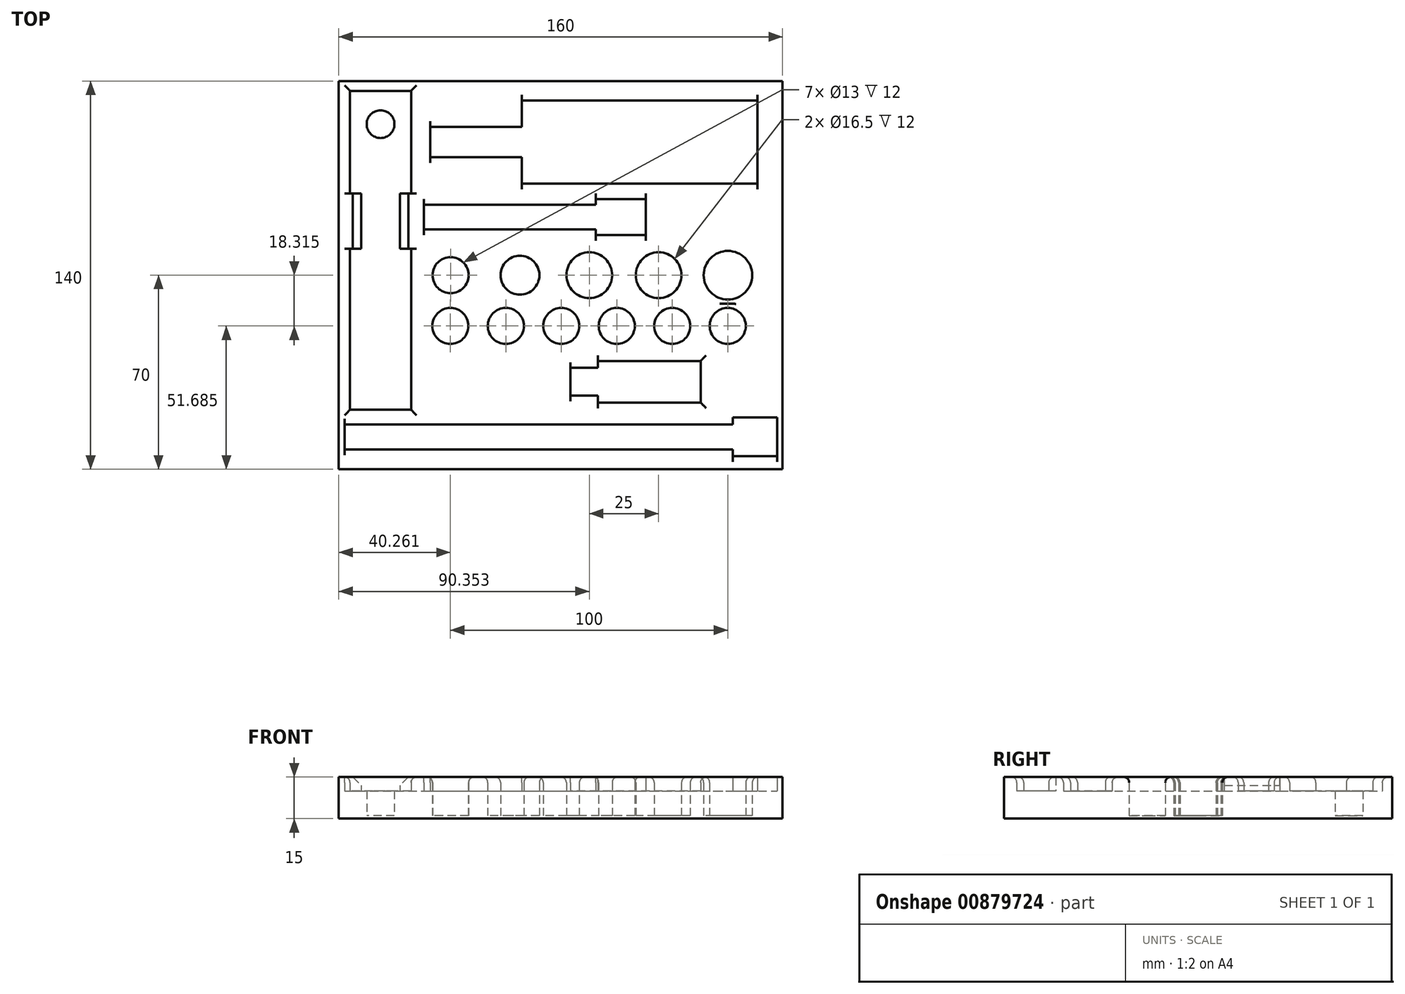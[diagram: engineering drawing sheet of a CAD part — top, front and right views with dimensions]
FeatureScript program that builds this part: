
annotation { "Feature Type Name" : "Feature", "Feature Type Description" : "" }
export const myFeature = defineFeature(function(context is Context, id is Id, definition is map)
    precondition{}
    {
        {
            var Q0;
            Q0=qCreatedBy(makeId("Top.planeOp"),FACE);
            var sketch = newSketch(context, id + "F0", { "sketchPlane" : qUnion([Q0])});
            skLineSegment(sketch, "E0.bottom", {"start": v(-80, 70) * mm, "end": v(80, 70) * mm});
            skLineSegment(sketch, "E0.top", {"start": v(-80, -70) * mm, "end": v(80, -70) * mm});
            skLineSegment(sketch, "E0.left", {"start": v(-80, 70) * mm, "end": v(-80, -70) * mm});
            skLineSegment(sketch, "E0.right", {"start": v(80, 70) * mm, "end": v(80, -70) * mm});
            skPoint(sketch, "E0.middle", {"position": v(0, 0) * mm});
            skCircle(sketch, "E1", {"center": v(60.26, -18.32) * mm, "radius": 6.5 * mm});
            skCircle(sketch, "E2", {"center": v(40.26, -18.32) * mm, "radius": 6.5 * mm});
            skCircle(sketch, "E3", {"center": v(20.26, -18.32) * mm, "radius": 6.5 * mm});
            skCircle(sketch, "E4", {"center": v(0.26, -18.32) * mm, "radius": 6.5 * mm});
            skCircle(sketch, "E5", {"center": v(-19.74, -18.32) * mm, "radius": 6.5 * mm});
            skCircle(sketch, "E6", {"center": v(-39.74, -18.32) * mm, "radius": 6.5 * mm});
            skCircle(sketch, "E7", {"center": v(60.35, 0) * mm, "radius": 8.75 * mm});
            skCircle(sketch, "E8", {"center": v(35.35, 0) * mm, "radius": 8.25 * mm});
            skCircle(sketch, "E9", {"center": v(10.35, 0) * mm, "radius": 8.25 * mm});
            skCircle(sketch, "E10", {"center": v(-14.65, 0) * mm, "radius": 7 * mm});
            skCircle(sketch, "E11", {"center": v(-39.65, 0) * mm, "radius": 6.5 * mm});
            skLineSegment(sketch, "E12.bottom", {"start": v(-75.9, 66.47) * mm, "end": v(-53.9, 66.47) * mm});
            skLineSegment(sketch, "E12.top", {"start": v(-75.9, -48.53) * mm, "end": v(-53.9, -48.53) * mm});
            skLineSegment(sketch, "E12.left", {"start": v(-75.9, 66.47) * mm, "end": v(-75.9, 29.47) * mm});
            skLineSegment(sketch, "E12.right", {"start": v(-53.9, 66.47) * mm, "end": v(-53.9, 29.47) * mm});
            skPoint(sketch, "E12.middle", {"position": v(-64.9, 8.97) * mm});
            skLineSegment(sketch, "E13", {"start": v(-53.9, 29.47) * mm, "end": v(-57.9, 29.47) * mm});
            skLineSegment(sketch, "E14", {"start": v(-57.9, 29.47) * mm, "end": v(-57.9, 9.47) * mm});
            skLineSegment(sketch, "E15", {"start": v(-57.9, 9.47) * mm, "end": v(-53.9, 9.47) * mm});
            skLineSegment(sketch, "E16", {"start": v(-53.9, 9.47) * mm, "end": v(-53.9, -48.53) * mm});
            skLineSegment(sketch, "E17", {"start": v(-75.9, 29.47) * mm, "end": v(-75.9, 29.47) * mm});
            skLineSegment(sketch, "E18", {"start": v(-71.9, 29.47) * mm, "end": v(-71.9, 9.47) * mm});
            skLineSegment(sketch, "E19", {"start": v(-71.9, 9.47) * mm, "end": v(-75.9, 9.47) * mm});
            skLineSegment(sketch, "E20", {"start": v(-75.9, 29.47) * mm, "end": v(-71.9, 29.47) * mm});
            skLineSegment(sketch, "E21", {"start": v(-75.9, 9.47) * mm, "end": v(-75.9, -48.53) * mm});
            skCircle(sketch, "E22", {"center": v(-64.9, 54.47) * mm, "radius": 5 * mm});
            skLineSegment(sketch, "E23.bottom", {"start": v(30.73, 14.47) * mm, "end": v(12.73, 14.47) * mm});
            skLineSegment(sketch, "E23.top", {"start": v(30.73, 27.47) * mm, "end": v(12.73, 27.47) * mm});
            skLineSegment(sketch, "E23.left", {"start": v(30.73, 14.47) * mm, "end": v(30.73, 27.47) * mm});
            skLineSegment(sketch, "E23.right", {"start": v(12.73, 14.47) * mm, "end": v(12.73, 16.47) * mm});
            skLineSegment(sketch, "E24.bottom", {"start": v(12.73, 16.47) * mm, "end": v(-49.27, 16.47) * mm});
            skLineSegment(sketch, "E24.top", {"start": v(12.73, 25.47) * mm, "end": v(-49.27, 25.47) * mm});
            skLineSegment(sketch, "E24.left", {"start": v(12.73, 16.47) * mm, "end": v(12.73, 16.47) * mm});
            skLineSegment(sketch, "E24.right", {"start": v(-49.27, 16.47) * mm, "end": v(-49.27, 25.47) * mm});
            skLineSegment(sketch, "E25", {"start": v(12.73, 25.47) * mm, "end": v(12.73, 25.47) * mm});
            skLineSegment(sketch, "E26", {"start": v(12.73, 25.47) * mm, "end": v(12.73, 27.47) * mm});
            skLineSegment(sketch, "E27.bottom", {"start": v(71, 33) * mm, "end": v(-14, 33) * mm});
            skLineSegment(sketch, "E27.top", {"start": v(71, 63) * mm, "end": v(-14, 63) * mm});
            skLineSegment(sketch, "E27.left", {"start": v(71, 33) * mm, "end": v(71, 63) * mm});
            skLineSegment(sketch, "E27.right", {"start": v(-14, 33) * mm, "end": v(-14, 42.5) * mm});
            skLineSegment(sketch, "E28.bottom", {"start": v(-14, 42.5) * mm, "end": v(-47, 42.5) * mm});
            skLineSegment(sketch, "E28.top", {"start": v(-14, 53.5) * mm, "end": v(-47, 53.5) * mm});
            skLineSegment(sketch, "E28.left", {"start": v(-14, 42.5) * mm, "end": v(-14, 42.5) * mm});
            skLineSegment(sketch, "E28.right", {"start": v(-47, 42.5) * mm, "end": v(-47, 53.5) * mm});
            skLineSegment(sketch, "E29", {"start": v(-14, 53.5) * mm, "end": v(-14, 53.5) * mm});
            skLineSegment(sketch, "E30.trimOffspring", {"start": v(-14, 53.5) * mm, "end": v(-14, 63) * mm});
            skLineSegment(sketch, "E31.bottom", {"start": v(78.13, -65.33) * mm, "end": v(62.13, -65.33) * mm});
            skLineSegment(sketch, "E31.top", {"start": v(78.13, -51.33) * mm, "end": v(62.13, -51.33) * mm});
            skLineSegment(sketch, "E31.left", {"start": v(78.13, -65.33) * mm, "end": v(78.13, -51.33) * mm});
            skLineSegment(sketch, "E31.right", {"start": v(62.13, -65.33) * mm, "end": v(62.13, -62.83) * mm});
            skLineSegment(sketch, "E32.bottom", {"start": v(62.13, -62.83) * mm, "end": v(-77.87, -62.83) * mm});
            skLineSegment(sketch, "E32.top", {"start": v(62.13, -53.83) * mm, "end": v(-77.87, -53.83) * mm});
            skLineSegment(sketch, "E32.left", {"start": v(62.13, -62.83) * mm, "end": v(62.13, -62.83) * mm});
            skLineSegment(sketch, "E32.right", {"start": v(-77.87, -62.83) * mm, "end": v(-77.87, -53.83) * mm});
            skLineSegment(sketch, "E33", {"start": v(62.13, -53.83) * mm, "end": v(62.13, -53.83) * mm});
            skLineSegment(sketch, "E34.trimOffspring", {"start": v(62.13, -53.83) * mm, "end": v(62.13, -51.33) * mm});
            skLineSegment(sketch, "E35", {"start": v(3.48, -33.45) * mm, "end": v(13.48, -33.45) * mm});
            skLineSegment(sketch, "E36", {"start": v(13.48, -33.45) * mm, "end": v(13.48, -30.95) * mm});
            skLineSegment(sketch, "E37", {"start": v(13.48, -30.95) * mm, "end": v(50.48, -30.95) * mm});
            skLineSegment(sketch, "E38", {"start": v(50.48, -30.95) * mm, "end": v(50.48, -45.95) * mm});
            skLineSegment(sketch, "E39", {"start": v(50.48, -45.95) * mm, "end": v(13.48, -45.95) * mm});
            skLineSegment(sketch, "E40", {"start": v(13.48, -45.95) * mm, "end": v(13.48, -43.45) * mm});
            skLineSegment(sketch, "E41", {"start": v(13.48, -43.45) * mm, "end": v(3.48, -43.45) * mm});
            skLineSegment(sketch, "E42", {"start": v(3.48, -43.45) * mm, "end": v(3.48, -33.45) * mm});
            skLineSegment(sketch, "E43", {"start": v(60.35, 0) * mm, "end": v(-39.65, 0) * mm, "construction": true});
            skLineSegment(sketch, "E44", {"start": v(60.26, -18.32) * mm, "end": v(-39.74, -18.32) * mm, "construction": true});
            skSolve(sketch);
        }
        {
            var Q0;
            Q0=makeQuery(id+"F0.imprint","IMPRINT",FACE,{"disambiguationData":[TD([[makeQuery(id+"F0.imprint","IMPRINT",EDGE,{"derivedFrom":sQuery(id+"F0.wireOp",EDGE,"E22")}),1.0]])]});
            var Q1;
            Q1=makeQuery(id+"F0.imprint","IMPRINT",FACE,{"disambiguationData":[TD([[makeQuery(id+"F0.imprint","IMPRINT",EDGE,{"derivedFrom":sQuery(id+"F0.wireOp",EDGE,"E11")}),1.0]])]});
            var Q2;
            Q2=makeQuery(id+"F0.imprint","IMPRINT",FACE,{"disambiguationData":[TD([[makeQuery(id+"F0.imprint","IMPRINT",EDGE,{"derivedFrom":sQuery(id+"F0.wireOp",EDGE,"E10")}),1.0]])]});
            var Q3;
            Q3=makeQuery(id+"F0.imprint","IMPRINT",FACE,{"disambiguationData":[TD([[makeQuery(id+"F0.imprint","IMPRINT",EDGE,{"derivedFrom":sQuery(id+"F0.wireOp",EDGE,"E9")}),1.0]])]});
            var Q4;
            Q4=makeQuery(id+"F0.imprint","IMPRINT",FACE,{"disambiguationData":[TD([[makeQuery(id+"F0.imprint","IMPRINT",EDGE,{"derivedFrom":sQuery(id+"F0.wireOp",EDGE,"E8")}),1.0]])]});
            var Q5;
            Q5=makeQuery(id+"F0.imprint","IMPRINT",FACE,{"disambiguationData":[TD([[makeQuery(id+"F0.imprint","IMPRINT",EDGE,{"derivedFrom":sQuery(id+"F0.wireOp",EDGE,"E7")}),1.0]])]});
            var Q6;
            Q6=makeQuery(id+"F0.imprint","IMPRINT",FACE,{"disambiguationData":[TD([[makeQuery(id+"F0.imprint","IMPRINT",EDGE,{"derivedFrom":sQuery(id+"F0.wireOp",EDGE,"E6")}),1.0]])]});
            var Q7;
            Q7=makeQuery(id+"F0.imprint","IMPRINT",FACE,{"disambiguationData":[TD([[makeQuery(id+"F0.imprint","IMPRINT",EDGE,{"derivedFrom":sQuery(id+"F0.wireOp",EDGE,"E5")}),1.0]])]});
            var Q8;
            Q8=makeQuery(id+"F0.imprint","IMPRINT",FACE,{"disambiguationData":[TD([[makeQuery(id+"F0.imprint","IMPRINT",EDGE,{"derivedFrom":sQuery(id+"F0.wireOp",EDGE,"E27.bottom")}),-1.0]])]});
            var Q9;
            Q9=makeQuery(id+"F0.imprint","IMPRINT",FACE,{"disambiguationData":[TD([[makeQuery(id+"F0.imprint","IMPRINT",EDGE,{"derivedFrom":sQuery(id+"F0.wireOp",EDGE,"E4")}),1.0]])]});
            var Q10;
            Q10=makeQuery(id+"F0.imprint","IMPRINT",FACE,{"disambiguationData":[TD([[makeQuery(id+"F0.imprint","IMPRINT",EDGE,{"derivedFrom":sQuery(id+"F0.wireOp",EDGE,"E23.bottom")}),-1.0]])]});
            var Q11;
            Q11=makeQuery(id+"F0.imprint","IMPRINT",FACE,{"disambiguationData":[TD([[makeQuery(id+"F0.imprint","IMPRINT",EDGE,{"derivedFrom":sQuery(id+"F0.wireOp",EDGE,"E3")}),1.0]])]});
            var Q12;
            Q12=makeQuery(id+"F0.imprint","IMPRINT",FACE,{"disambiguationData":[TD([[makeQuery(id+"F0.imprint","IMPRINT",EDGE,{"derivedFrom":sQuery(id+"F0.wireOp",EDGE,"E12.bottom")}),-1.0]])]});
            var Q13;
            Q13=makeQuery(id+"F0.imprint","IMPRINT",FACE,{"disambiguationData":[TD([[makeQuery(id+"F0.imprint","IMPRINT",EDGE,{"derivedFrom":sQuery(id+"F0.wireOp",EDGE,"n4SuDj0L-OX6M-LfaT-G9qN-pV2BYgX4VWdp.bottom")}),-1.0]])]});
            var Q14;
            Q14=makeQuery(id+"F0.imprint","IMPRINT",FACE,{"disambiguationData":[TD([[makeQuery(id+"F0.imprint","IMPRINT",EDGE,{"derivedFrom":sQuery(id+"F0.wireOp",EDGE,"E2")}),1.0]])]});
            var Q15;
            Q15=makeQuery(id+"F0.imprint","IMPRINT",FACE,{"disambiguationData":[TD([[makeQuery(id+"F0.imprint","IMPRINT",EDGE,{"derivedFrom":sQuery(id+"F0.wireOp",EDGE,"E31.bottom")}),-1.0]])]});
            var Q16;
            Q16=makeQuery(id+"F0.imprint","IMPRINT",FACE,{"disambiguationData":[TD([[makeQuery(id+"F0.imprint","IMPRINT",EDGE,{"derivedFrom":sQuery(id+"F0.wireOp",EDGE,"E0.bottom")}),-1.0]])]});
            var Q17;
            Q17=makeQuery(id+"F0.imprint","IMPRINT",FACE,{"disambiguationData":[TD([[makeQuery(id+"F0.imprint","IMPRINT",EDGE,{"derivedFrom":sQuery(id+"F0.wireOp",EDGE,"E1")}),1.0]])]});
            var Q18;
            Q18=makeQuery(id+"F0.imprint","IMPRINT",FACE,{"disambiguationData":[TD([[makeQuery(id+"F0.imprint","IMPRINT",EDGE,{"derivedFrom":sQuery(id+"F0.wireOp",EDGE,"E35")}),-1.0]])]});
            extrude(context, id + "F1", {"entities" : qUnion([Q0, Q1, Q2, Q3, Q4, Q5, Q6, Q7, Q8, Q9, Q10, Q11, Q12, Q13, Q14, Q15, Q16, Q17, Q18]), "depth" : 1 * mm, "offsetDistance" : 25 * mm});
        }
        {
            var Q0;
            Q0=makeQuery(id+"F0.imprint","IMPRINT",FACE,{"disambiguationData":[TD([[makeQuery(id+"F0.imprint","IMPRINT",EDGE,{"derivedFrom":sQuery(id+"F0.wireOp",EDGE,"E0.bottom")}),-1.0]])]});
            var Q1;
            Q1=makeQuery(id+"F0.imprint","IMPRINT",FACE,{"disambiguationData":[TD([[makeQuery(id+"F0.imprint","IMPRINT",EDGE,{"derivedFrom":sQuery(id+"F0.wireOp",EDGE,"n4SuDj0L-OX6M-LfaT-G9qN-pV2BYgX4VWdp.bottom")}),-1.0]])]});
            var Q2;
            Q2=makeQuery(id+"F0.imprint","IMPRINT",FACE,{"disambiguationData":[TD([[makeQuery(id+"F0.imprint","IMPRINT",EDGE,{"derivedFrom":sQuery(id+"F0.wireOp",EDGE,"E31.bottom")}),-1.0]])]});
            var Q3;
            Q3=makeQuery(id+"F0.imprint","IMPRINT",FACE,{"disambiguationData":[TD([[makeQuery(id+"F0.imprint","IMPRINT",EDGE,{"derivedFrom":sQuery(id+"F0.wireOp",EDGE,"E12.bottom")}),-1.0]])]});
            var Q4;
            Q4=makeQuery(id+"F0.imprint","IMPRINT",FACE,{"disambiguationData":[TD([[makeQuery(id+"F0.imprint","IMPRINT",EDGE,{"derivedFrom":sQuery(id+"F0.wireOp",EDGE,"E23.bottom")}),-1.0]])]});
            var Q5;
            Q5=makeQuery(id+"F0.imprint","IMPRINT",FACE,{"disambiguationData":[TD([[makeQuery(id+"F0.imprint","IMPRINT",EDGE,{"derivedFrom":sQuery(id+"F0.wireOp",EDGE,"E35")}),-1.0]])]});
            var Q6;
            Q6=makeQuery(id+"F0.imprint","IMPRINT",FACE,{"disambiguationData":[TD([[makeQuery(id+"F0.imprint","IMPRINT",EDGE,{"derivedFrom":sQuery(id+"F0.wireOp",EDGE,"E27.bottom")}),-1.0]])]});
            extrude(context, id + "F2", {"entities" : qUnion([Q0, Q1, Q2, Q3, Q4, Q5, Q6]), "operationType" : NewBodyOperationType.ADD, "depth" : 10 * mm, "offsetDistance" : 25 * mm});
        }
        {
            var Q0;
            Q0=makeQuery(id+"F0.imprint","IMPRINT",FACE,{"disambiguationData":[TD([[makeQuery(id+"F0.imprint","IMPRINT",EDGE,{"derivedFrom":sQuery(id+"F0.wireOp",EDGE,"E0.bottom")}),-1.0]])]});
            extrude(context, id + "F3", {"entities" : qUnion([Q0]), "operationType" : NewBodyOperationType.ADD, "depth" : 15 * mm, "offsetDistance" : 25 * mm});
        }
        {
            var Q0;
            Q0=makeQuery(id+"F3.opExtrude","CAP_EDGE",EDGE,{"disambiguationData":[OSD([sQuery(id+"F0.wireOp",EDGE,"E14")])],"isStart":false});
            var Q1;
            Q1=makeQuery(id+"F3.opExtrude","CAP_EDGE",EDGE,{"disambiguationData":[OSD([sQuery(id+"F0.wireOp",EDGE,"E18")])],"isStart":false});
            chamfer(context, id + "F4", {"entities" : qUnion([Q0, Q1]), "width" : 3 * mm, "tangentPropagation" : true});
        }
        {
            var Q0;
            Q0=makeQuery(id+"F3.opExtrude","CAP_EDGE",EDGE,{"disambiguationData":[OSD([sQuery(id+"F0.wireOp",EDGE,"E12.left")])],"isStart":false});
            var Q1;
            Q1=makeQuery(id+"F3.opExtrude","CAP_EDGE",EDGE,{"disambiguationData":[OSD([sQuery(id+"F0.wireOp",EDGE,"E12.right")])],"isStart":false});
            var Q2;
            Q2=makeQuery(id+"F3.opExtrude","CAP_EDGE",EDGE,{"disambiguationData":[OSD([sQuery(id+"F0.wireOp",EDGE,"E16")])],"isStart":false});
            var Q3;
            Q3=makeQuery(id+"F3.opExtrude","CAP_EDGE",EDGE,{"disambiguationData":[OSD([sQuery(id+"F0.wireOp",EDGE,"E21")])],"isStart":false});
            var Q4;
            Q4=makeQuery(id+"F3.opExtrude","CAP_EDGE",EDGE,{"disambiguationData":[OSD([sQuery(id+"F0.wireOp",EDGE,"E12.top")])],"isStart":false});
            var Q5;
            Q5=makeQuery(id+"F3.opExtrude","CAP_EDGE",EDGE,{"disambiguationData":[OSD([sQuery(id+"F0.wireOp",EDGE,"E12.bottom")])],"isStart":false});
            var Q6;
            Q6=makeQuery(id+"F3.opExtrude","CAP_EDGE",EDGE,{"disambiguationData":[OSD([sQuery(id+"F0.wireOp",EDGE,"E32.bottom")])],"isStart":false});
            var Q7;
            Q7=makeQuery(id+"F3.opExtrude","CAP_EDGE",EDGE,{"disambiguationData":[OSD([sQuery(id+"F0.wireOp",EDGE,"E31.bottom")])],"isStart":false});
            var Q8;
            Q8=makeQuery(id+"F3.opExtrude","CAP_EDGE",EDGE,{"disambiguationData":[OSD([sQuery(id+"F0.wireOp",EDGE,"E27.top")])],"isStart":false});
            var Q9;
            Q9=makeQuery(id+"F3.opExtrude","CAP_EDGE",EDGE,{"disambiguationData":[OSD([sQuery(id+"F0.wireOp",EDGE,"E27.bottom")])],"isStart":false});
            var Q10;
            Q10=makeQuery(id+"F3.opExtrude","CAP_EDGE",EDGE,{"disambiguationData":[OSD([sQuery(id+"F0.wireOp",EDGE,"E28.bottom")])],"isStart":false});
            var Q11;
            Q11=makeQuery(id+"F3.opExtrude","CAP_EDGE",EDGE,{"disambiguationData":[OSD([sQuery(id+"F0.wireOp",EDGE,"E28.top")])],"isStart":false});
            var Q12;
            Q12=makeQuery(id+"F3.opExtrude","CAP_EDGE",EDGE,{"disambiguationData":[OSD([sQuery(id+"F0.wireOp",EDGE,"E23.top")])],"isStart":false});
            var Q13;
            Q13=makeQuery(id+"F3.opExtrude","CAP_EDGE",EDGE,{"disambiguationData":[OSD([sQuery(id+"F0.wireOp",EDGE,"E23.bottom")])],"isStart":false});
            var Q14;
            Q14=makeQuery(id+"F3.opExtrude","CAP_EDGE",EDGE,{"disambiguationData":[OSD([sQuery(id+"F0.wireOp",EDGE,"E24.bottom")])],"isStart":false});
            var Q15;
            Q15=makeQuery(id+"F3.opExtrude","CAP_EDGE",EDGE,{"disambiguationData":[OSD([sQuery(id+"F0.wireOp",EDGE,"E24.top")])],"isStart":false});
            var Q16;
            Q16=makeQuery(id+"F3.opExtrude","CAP_EDGE",EDGE,{"disambiguationData":[OSD([sQuery(id+"F0.wireOp",EDGE,"aEfjKwd9-Bmm9-NIEr-MqMZ-lCz7Br84sUfY.bottom")])],"isStart":false});
            var Q17;
            Q17=makeQuery(id+"F3.opExtrude","CAP_EDGE",EDGE,{"disambiguationData":[OSD([sQuery(id+"F0.wireOp",EDGE,"aEfjKwd9-Bmm9-NIEr-MqMZ-lCz7Br84sUfY.top")])],"isStart":false});
            var Q18;
            Q18=makeQuery(id+"F3.opExtrude","CAP_EDGE",EDGE,{"disambiguationData":[OSD([sQuery(id+"F0.wireOp",EDGE,"n4SuDj0L-OX6M-LfaT-G9qN-pV2BYgX4VWdp.bottom")])],"isStart":false});
            var Q19;
            Q19=makeQuery(id+"F3.opExtrude","CAP_EDGE",EDGE,{"disambiguationData":[OSD([sQuery(id+"F0.wireOp",EDGE,"n4SuDj0L-OX6M-LfaT-G9qN-pV2BYgX4VWdp.top")])],"isStart":false});
            var Q20;
            Q20=makeQuery(id+"F3.opExtrude","CAP_EDGE",EDGE,{"disambiguationData":[OSD([sQuery(id+"F0.wireOp",EDGE,"E11")])],"isStart":false});
            var Q21;
            Q21=makeQuery(id+"F3.opExtrude","CAP_EDGE",EDGE,{"disambiguationData":[OSD([sQuery(id+"F0.wireOp",EDGE,"E10")])],"isStart":false});
            var Q22;
            Q22=makeQuery(id+"F3.opExtrude","CAP_EDGE",EDGE,{"disambiguationData":[OSD([sQuery(id+"F0.wireOp",EDGE,"E9")])],"isStart":false});
            var Q23;
            Q23=makeQuery(id+"F3.opExtrude","CAP_EDGE",EDGE,{"disambiguationData":[OSD([sQuery(id+"F0.wireOp",EDGE,"E8")])],"isStart":false});
            var Q24;
            Q24=makeQuery(id+"F3.opExtrude","CAP_EDGE",EDGE,{"disambiguationData":[OSD([sQuery(id+"F0.wireOp",EDGE,"E7")])],"isStart":false});
            var Q25;
            Q25=makeQuery(id+"F3.opExtrude","CAP_EDGE",EDGE,{"disambiguationData":[OSD([sQuery(id+"F0.wireOp",EDGE,"E1")])],"isStart":false});
            var Q26;
            Q26=makeQuery(id+"F3.opExtrude","CAP_EDGE",EDGE,{"disambiguationData":[OSD([sQuery(id+"F0.wireOp",EDGE,"E2")])],"isStart":false});
            var Q27;
            Q27=makeQuery(id+"F3.opExtrude","CAP_EDGE",EDGE,{"disambiguationData":[OSD([sQuery(id+"F0.wireOp",EDGE,"E3")])],"isStart":false});
            var Q28;
            Q28=makeQuery(id+"F3.opExtrude","CAP_EDGE",EDGE,{"disambiguationData":[OSD([sQuery(id+"F0.wireOp",EDGE,"E4")])],"isStart":false});
            var Q29;
            Q29=makeQuery(id+"F3.opExtrude","CAP_EDGE",EDGE,{"disambiguationData":[OSD([sQuery(id+"F0.wireOp",EDGE,"E5")])],"isStart":false});
            var Q30;
            Q30=makeQuery(id+"F3.opExtrude","CAP_EDGE",EDGE,{"disambiguationData":[OSD([sQuery(id+"F0.wireOp",EDGE,"E6")])],"isStart":false});
            var Q31;
            Q31=makeQuery(id+"F3.opExtrude","CAP_EDGE",EDGE,{"disambiguationData":[OSD([sQuery(id+"F0.wireOp",EDGE,"E37")])],"isStart":false});
            var Q32;
            Q32=makeQuery(id+"F3.opExtrude","CAP_EDGE",EDGE,{"disambiguationData":[OSD([sQuery(id+"F0.wireOp",EDGE,"E39")])],"isStart":false});
            var Q33;
            Q33=makeQuery(id+"F3.opExtrude","CAP_EDGE",EDGE,{"disambiguationData":[OSD([sQuery(id+"F0.wireOp",EDGE,"E32.top")])],"isStart":false});
            var Q34;
            Q34=makeQuery(id+"F3.opExtrude","CAP_EDGE",EDGE,{"disambiguationData":[OSD([sQuery(id+"F0.wireOp",EDGE,"E41")])],"isStart":false});
            var Q35;
            Q35=makeQuery(id+"F3.opExtrude","CAP_EDGE",EDGE,{"disambiguationData":[OSD([sQuery(id+"F0.wireOp",EDGE,"E35")])],"isStart":false});
            var Q36;
            Q36=makeQuery(id+"F3.opExtrude","CAP_EDGE",EDGE,{"disambiguationData":[OSD([sQuery(id+"F0.wireOp",EDGE,"E38")])],"isStart":false});
            fillet(context, id + "F5", {"entities" : qUnion([Q0, Q1, Q2, Q3, Q4, Q5, Q6, Q7, Q8, Q9, Q10, Q11, Q12, Q13, Q14, Q15, Q16, Q17, Q18, Q19, Q20, Q21, Q22, Q23, Q24, Q25, Q26, Q27, Q28, Q29, Q30, Q31, Q32, Q33, Q34, Q35, Q36]), "tangentPropagation" : true, "radius" : 2 * mm, "defaultsChanged" : false, "vertexSettings" : [], "allowEdgeOverflow" : false});
        }
    });
